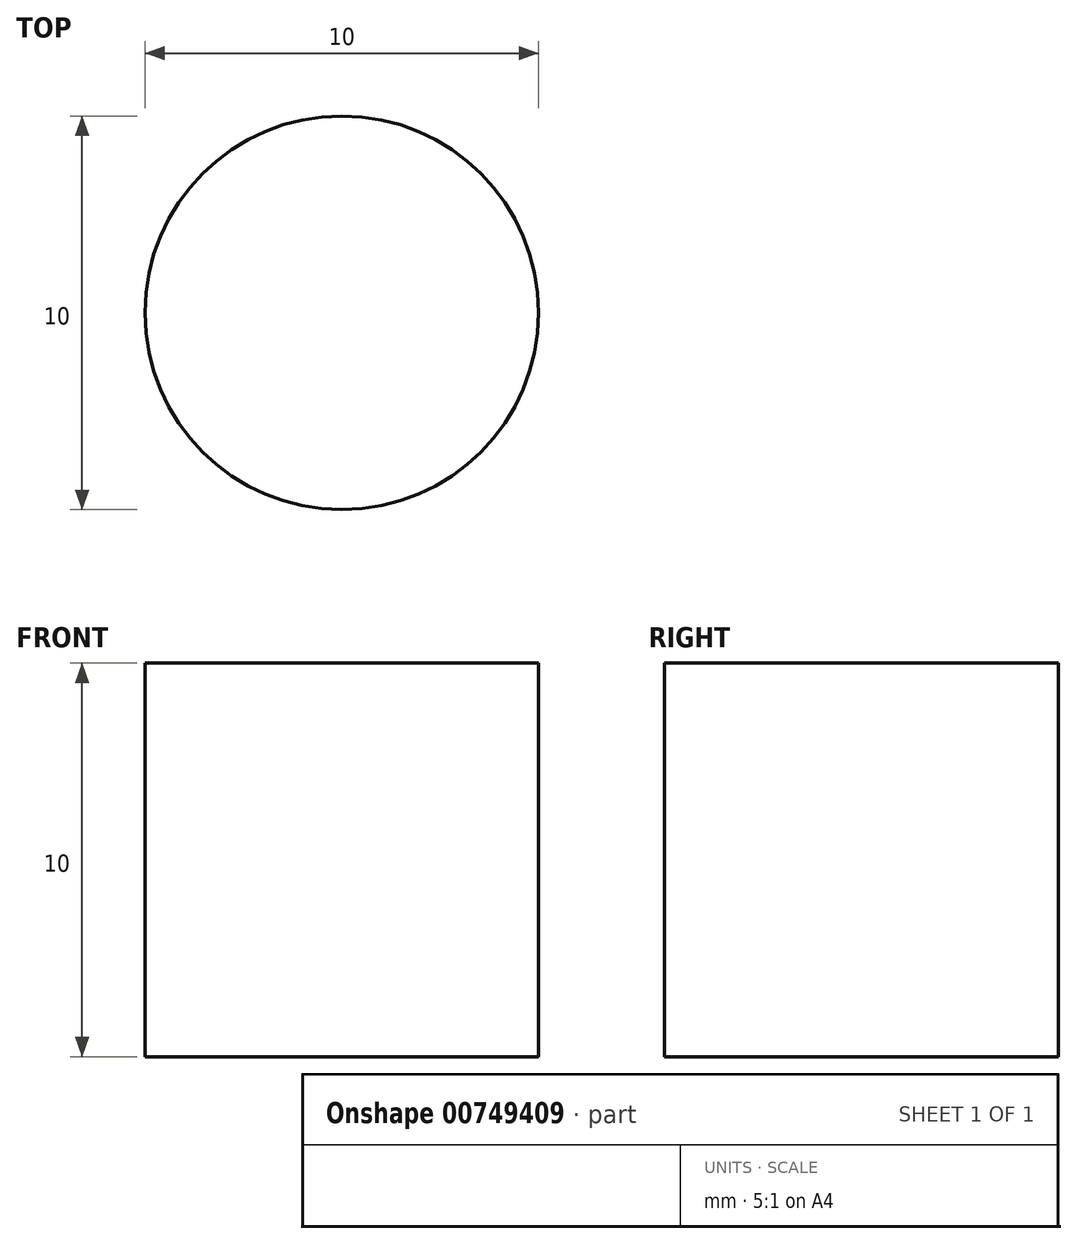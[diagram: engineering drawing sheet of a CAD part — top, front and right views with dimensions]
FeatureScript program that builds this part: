
annotation { "Feature Type Name" : "Feature", "Feature Type Description" : "" }
export const myFeature = defineFeature(function(context is Context, id is Id, definition is map)
    precondition{}
    {
        {
            var Q0;
            Q0=qCreatedBy(makeId("Top.planeOp"),FACE);
            var sketch = newSketch(context, id + "F0", { "sketchPlane" : qUnion([Q0])});
            skCircle(sketch, "E0", {"center": v(0, 0) * mm, "radius": 5 * mm});
            skSolve(sketch);
        }
        {
            var Q0;
            Q0 = qSketchRegion(id + "F0", true);
            extrude(context, id + "F1", {"entities" : qUnion([Q0]), "endBound" : BoundingType.SYMMETRIC, "depth" : 10 * mm, "offsetDistance" : 25 * mm});
        }
    });
